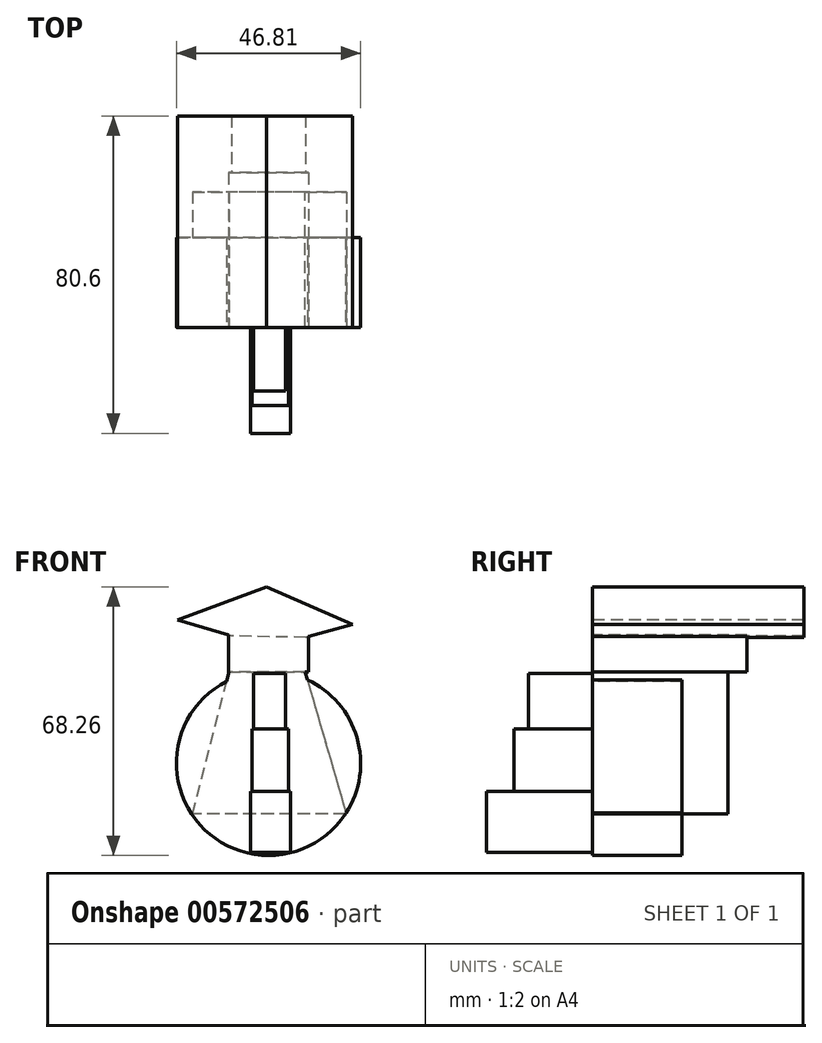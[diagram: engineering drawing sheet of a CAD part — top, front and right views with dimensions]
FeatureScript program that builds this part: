
annotation { "Feature Type Name" : "Feature", "Feature Type Description" : "" }
export const myFeature = defineFeature(function(context is Context, id is Id, definition is map)
    precondition{}
    {
        {
            var Q0;
            Q0=qCreatedBy(makeId("Front.planeOp"),FACE);
            var sketch = newSketch(context, id + "F0", { "sketchPlane" : qUnion([Q0])});
            skLineSegment(sketch, "E0.bottom", {"start": v(-42.46, -15.79) * mm, "end": v(-32.3, -15.79) * mm});
            skLineSegment(sketch, "E0.top", {"start": v(-42.46, -31.4) * mm, "end": v(-32.3, -31.4) * mm});
            skLineSegment(sketch, "E0.left", {"start": v(-42.46, -15.79) * mm, "end": v(-42.46, -31.4) * mm});
            skLineSegment(sketch, "E0.right", {"start": v(-32.3, -15.79) * mm, "end": v(-32.3, -31.4) * mm});
            skSolve(sketch);
        }
        {
            var Q0;
            Q0 = qSketchRegion(id + "F0", true);
            extrude(context, id + "F1", {"entities" : qUnion([Q0]), "depth" : 26.9 * mm, "offsetDistance" : 25 * mm});
        }
        {
            var Q0;
            Q0=qCreatedBy(makeId("Front.planeOp"),FACE);
            var sketch = newSketch(context, id + "F2", { "sketchPlane" : qUnion([Q0])});
            skLineSegment(sketch, "E1.bottom", {"start": v(-42.1, 0) * mm, "end": v(-32.84, 0) * mm});
            skLineSegment(sketch, "E1.top", {"start": v(-42.1, -16.51) * mm, "end": v(-32.84, -16.51) * mm});
            skLineSegment(sketch, "E1.left", {"start": v(-42.1, 0) * mm, "end": v(-42.1, -16.51) * mm});
            skLineSegment(sketch, "E1.right", {"start": v(-32.84, 0) * mm, "end": v(-32.84, -16.51) * mm});
            skSolve(sketch);
        }
        {
            var Q0;
            Q0 = qSketchRegion(id + "F2", true);
            extrude(context, id + "F3", {"entities" : qUnion([Q0]), "operationType" : NewBodyOperationType.ADD, "depth" : 19.9 * mm, "offsetDistance" : 25 * mm});
        }
        {
            var Q0;
            Q0=qCreatedBy(makeId("Front.planeOp"),FACE);
            var sketch = newSketch(context, id + "F4", { "sketchPlane" : qUnion([Q0])});
            skLineSegment(sketch, "E2.bottom", {"start": v(-41.73, 0) * mm, "end": v(-33.57, 0) * mm});
            skLineSegment(sketch, "E2.top", {"start": v(-41.73, 14.15) * mm, "end": v(-33.57, 14.15) * mm});
            skLineSegment(sketch, "E2.left", {"start": v(-41.73, 0) * mm, "end": v(-41.73, 14.15) * mm});
            skLineSegment(sketch, "E2.right", {"start": v(-33.57, 0) * mm, "end": v(-33.57, 14.15) * mm});
            skSolve(sketch);
        }
        {
            var Q0;
            Q0 = qSketchRegion(id + "F4", true);
            extrude(context, id + "F5", {"entities" : qUnion([Q0]), "operationType" : NewBodyOperationType.ADD, "depth" : 16.2 * mm, "offsetDistance" : 25 * mm});
        }
        {
            var Q0;
            Q0=qCreatedBy(makeId("Front.planeOp"),FACE);
            var sketch = newSketch(context, id + "F6", { "sketchPlane" : qUnion([Q0])});
            skCircle(sketch, "E3", {"center": v(-37.92, -8.7) * mm, "radius": 23.4 * mm});
            skSolve(sketch);
        }
        {
            var Q0;
            Q0 = qSketchRegion(id + "F6", true);
            extrude(context, id + "F7", {"entities" : qUnion([Q0]), "operationType" : NewBodyOperationType.ADD, "oppositeDirection" : true, "depth" : 22.8 * mm, "offsetDistance" : 25 * mm});
        }
        {
            var Q0;
            Q0=qCreatedBy(makeId("Front.planeOp"),FACE);
            var sketch = newSketch(context, id + "F8", { "sketchPlane" : qUnion([Q0])});
            skLineSegment(sketch, "E4.bottom", {"start": v(-48.08, 14.52) * mm, "end": v(-27.76, 14.52) * mm});
            skLineSegment(sketch, "E4.top", {"start": v(-48.08, 24.86) * mm, "end": v(-27.76, 24.86) * mm});
            skLineSegment(sketch, "E4.left", {"start": v(-48.08, 14.52) * mm, "end": v(-48.08, 24.86) * mm});
            skLineSegment(sketch, "E4.right", {"start": v(-27.76, 14.52) * mm, "end": v(-27.76, 24.86) * mm});
            skSolve(sketch);
        }
        {
            var Q0;
            Q0 = qSketchRegion(id + "F8", true);
            extrude(context, id + "F9", {"entities" : qUnion([Q0]), "operationType" : NewBodyOperationType.ADD, "oppositeDirection" : true, "depth" : 39.3 * mm, "offsetDistance" : 25 * mm});
        }
        {
            var Q0;
            Q0=qCreatedBy(makeId("Front.planeOp"),FACE);
            var sketch = newSketch(context, id + "F10", { "sketchPlane" : qUnion([Q0])});
            skLineSegment(sketch, "E5", {"start": v(-47.34, 23.63) * mm, "end": v(-61.03, 27.66) * mm});
            skLineSegment(sketch, "E6", {"start": v(-61.03, 27.66) * mm, "end": v(-38.47, 36.14) * mm});
            skLineSegment(sketch, "E7", {"start": v(-38.47, 36.14) * mm, "end": v(-16.58, 26.59) * mm});
            skLineSegment(sketch, "E8", {"start": v(-16.58, 26.59) * mm, "end": v(-28.47, 23.28) * mm});
            skLineSegment(sketch, "E9", {"start": v(-28.47, 23.28) * mm, "end": v(-47.34, 23.63) * mm});
            skSolve(sketch);
        }
        {
            var Q0;
            Q0 = qSketchRegion(id + "F10", true);
            extrude(context, id + "F11", {"entities" : qUnion([Q0]), "operationType" : NewBodyOperationType.ADD, "oppositeDirection" : true, "depth" : 53.7 * mm, "offsetDistance" : 25 * mm});
        }
        {
            var Q0;
            Q0=qCreatedBy(makeId("Front.planeOp"),FACE);
            var sketch = newSketch(context, id + "F12", { "sketchPlane" : qUnion([Q0])});
            skLineSegment(sketch, "E10", {"start": v(-28.85, 15.24) * mm, "end": v(-18.15, -21.6) * mm});
            skLineSegment(sketch, "E11", {"start": v(-18.15, -21.6) * mm, "end": v(-57.16, -21.6) * mm});
            skLineSegment(sketch, "E12", {"start": v(-57.16, -21.6) * mm, "end": v(-47.72, 15.42) * mm});
            skLineSegment(sketch, "E13", {"start": v(-47.72, 15.42) * mm, "end": v(-28.85, 15.24) * mm});
            skSolve(sketch);
        }
        {
            var Q0;
            Q0 = qSketchRegion(id + "F12", true);
            extrude(context, id + "F13", {"entities" : qUnion([Q0]), "operationType" : NewBodyOperationType.ADD, "oppositeDirection" : true, "depth" : 34.4 * mm, "offsetDistance" : 25 * mm});
        }
    });
